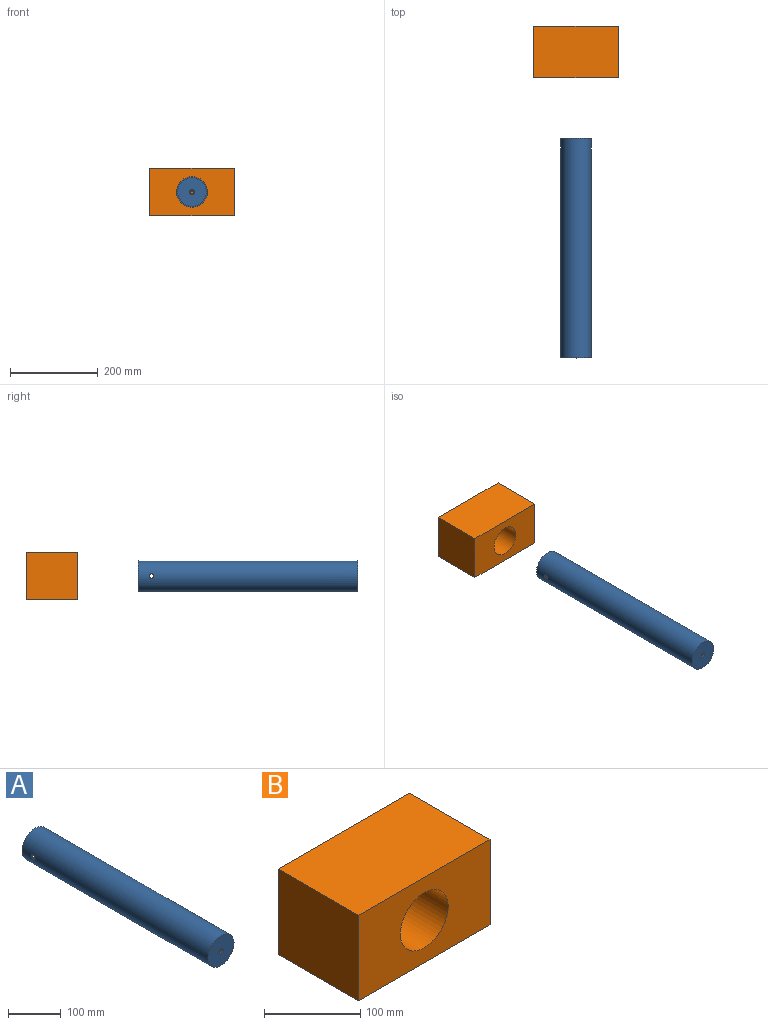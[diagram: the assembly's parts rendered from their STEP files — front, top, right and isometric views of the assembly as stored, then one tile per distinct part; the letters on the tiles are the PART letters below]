
ASSEMBLY  parts=2 mates=1
PART A: 8 faces, bbox 70x500x70 mm
  f0: cylinder r=35mm len=500mm, axis (0,1,0), area 109798.3mm2, adj f1,f2,f5,f6
  f1: plane 70x70mm, normal (0,-1,0), area 3749.9mm2, adj f0,f7
  f2: plane 70x70mm, normal (0,1,0), area 530.1mm2, adj f0,f3
  f3: cylinder r=32.5mm len=497.5mm, axis (0,1,0), area 101433.8mm2, adj f2,f4,f5,f6
  f4: plane 65x65mm, normal (0,1,0), area 3288.1mm2, adj f3,f7
  f5: cylinder r=5mm len=10mm, axis (1,0,0), area 79mm2, adj f0,f3
  f6: cylinder r=5mm len=10mm, axis (1,0,0), area 79mm2, adj f0,f3
  f7: cone r=2.5mm half-angle=45deg, axis (0,-1,0), area 96.6mm2, adj f1,f4
PART B: 8 faces, bbox 192.8x118x108.4 mm
  f0: plane 192.81x118mm, normal (0,0,-1), area 22751.2mm2, adj f1,f3,f4,f5
  f1: plane 118x108.43mm, normal (1,0,0), area 12795.1mm2, adj f0,f2,f4,f5
  f2: plane 192.81x118mm, normal (0,0,1), area 22751.2mm2, adj f1,f3,f4,f5
  f3: plane 118x108.43mm, normal (-1,0,0), area 12795.1mm2, adj f0,f2,f4,f5
  f4: plane 192.81x108.43mm, normal (0,-1,0), area 17058.1mm2, adj f0,f1,f2,f3,f6
  f5: plane 192.81x108.43mm, normal (0,1,0), area 20906.6mm2, adj f0,f1,f2,f3
  f6: cylinder r=35mm len=85mm, axis (0,-1,0), area 18692.5mm2, adj f4,f7
  f7: plane 70x70mm, normal (0,-1,0), area 3848.5mm2, adj f6
PLACE A t=(26.91,-45.63,21.88)mm
PLACE B t=(26.91,209.21,21.88)mm
MATE slider A.f0 <-> B.f6  axis (0,1,0) through (26.91,-45.63,21.88)mm
